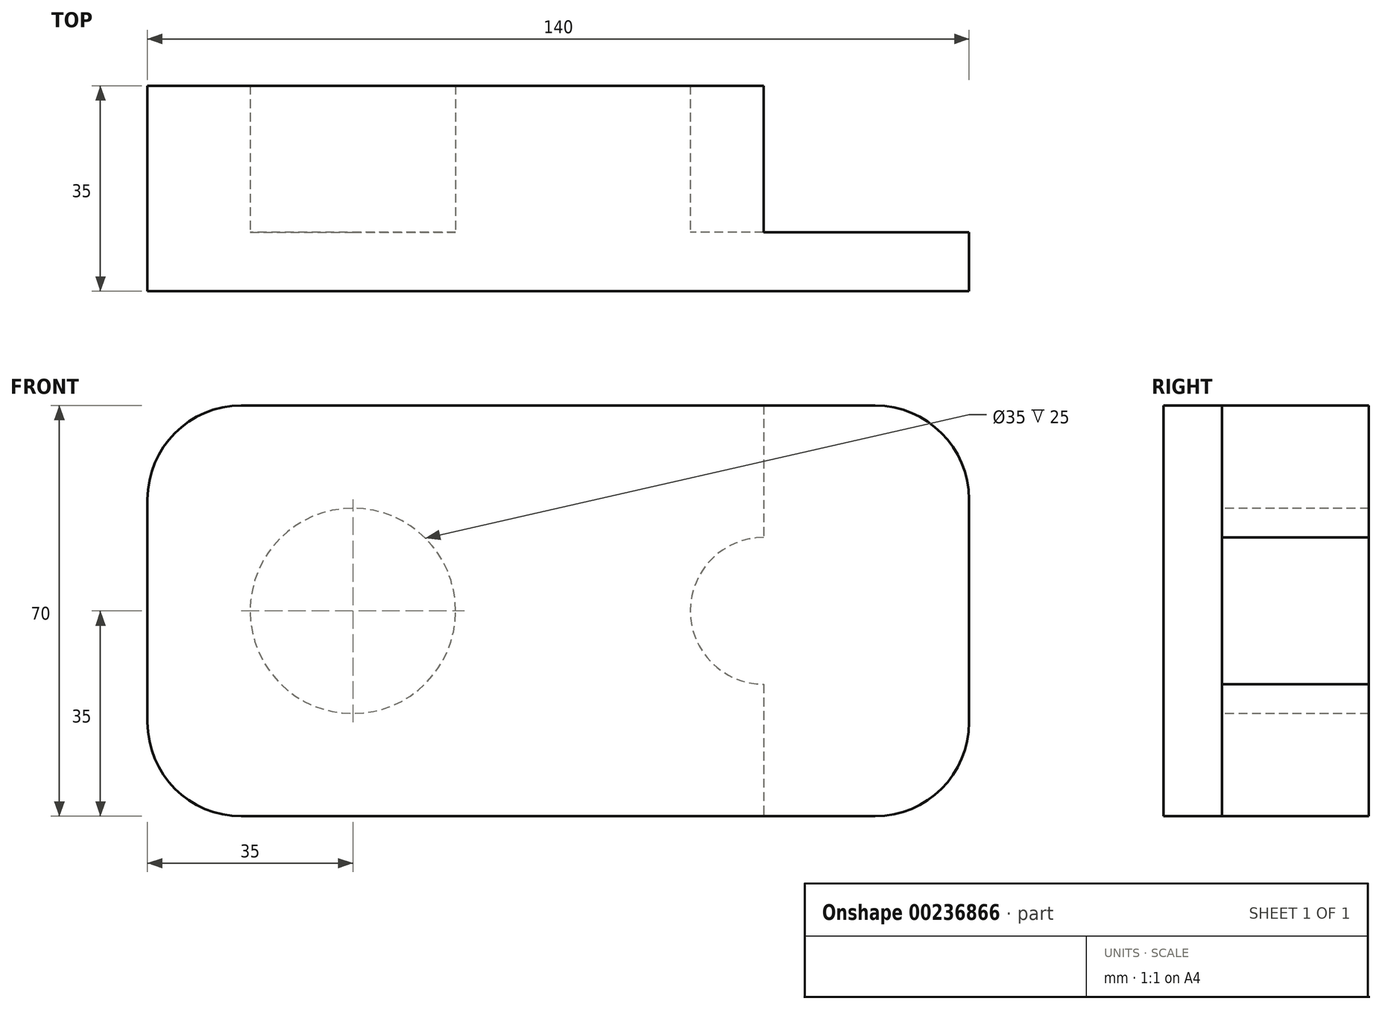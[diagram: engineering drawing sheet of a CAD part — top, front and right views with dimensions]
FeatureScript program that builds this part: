
annotation { "Feature Type Name" : "Feature", "Feature Type Description" : "" }
export const myFeature = defineFeature(function(context is Context, id is Id, definition is map)
    precondition{}
    {
        {
            var Q0;
            Q0=qCreatedBy(makeId("Front.planeOp"),FACE);
            var sketch = newSketch(context, id + "F0", { "sketchPlane" : qUnion([Q0])});
            skLineSegment(sketch, "E0", {"start": v(0, 0) * mm, "end": v(140, 0) * mm});
            skLineSegment(sketch, "E1", {"start": v(140, 0) * mm, "end": v(140, 70) * mm});
            skLineSegment(sketch, "E2", {"start": v(140, 70) * mm, "end": v(0, 70) * mm});
            skLineSegment(sketch, "E3", {"start": v(0, 70) * mm, "end": v(0, 0) * mm});
            skSolve(sketch);
        }
        {
            var Q0;
            Q0=makeQuery(id+"F0.imprint","IMPRINT",FACE,{"disambiguationData":[TD([[makeQuery(id+"F0.imprint","IMPRINT",EDGE,{"derivedFrom":sQuery(id+"F0.wireOp",EDGE,"E0")}),1.0]])]});
            extrude(context, id + "F1", {"entities" : qUnion([Q0]), "depth" : 10 * mm});
        }
        {
            var Q0;
            Q0=makeQuery(id+"F1.opExtrude","SWEPT_EDGE",EDGE,{"disambiguationData":[OSD([sQuery(id+"F0.wireOp",EDGE,"E0"),sQuery(id+"F0.wireOp",EDGE,"E3")])]});
            var Q1;
            Q1=makeQuery(id+"F1.opExtrude","SWEPT_EDGE",EDGE,{"disambiguationData":[OSD([sQuery(id+"F0.wireOp",EDGE,"E0"),sQuery(id+"F0.wireOp",EDGE,"E1")])]});
            var Q2;
            Q2=makeQuery(id+"F1.opExtrude","SWEPT_EDGE",EDGE,{"disambiguationData":[OSD([sQuery(id+"F0.wireOp",EDGE,"E1"),sQuery(id+"F0.wireOp",EDGE,"E2")])]});
            var Q3;
            Q3=makeQuery(id+"F1.opExtrude","SWEPT_EDGE",EDGE,{"disambiguationData":[OSD([sQuery(id+"F0.wireOp",EDGE,"E2"),sQuery(id+"F0.wireOp",EDGE,"E3")])]});
            fillet(context, id + "F2", {"entities" : qUnion([Q0, Q1, Q2, Q3]), "radius" : 16 * mm, "tangentPropagation" : true, "allowEdgeOverflow" : false});
        }
        {
            var Q0;
            Q0=makeQuery(id+"F1.opExtrude","CAP_FACE",FACE,{"disambiguationData":[OSD([sQuery(id+"F0.wireOp",EDGE,"E0"),sQuery(id+"F0.wireOp",EDGE,"E1"),sQuery(id+"F0.wireOp",EDGE,"E2"),sQuery(id+"F0.wireOp",EDGE,"E3")])],"isStart":true});
            var sketch = newSketch(context, id + "F3", { "sketchPlane" : qUnion([Q0])});
            skLineSegment(sketch, "E4", {"start": v(-140, 35) * mm, "end": v(0, 35) * mm});
            skLineSegment(sketch, "E5", {"start": v(-105, 70) * mm, "end": v(-105, 0) * mm});
            skLineSegment(sketch, "E6", {"start": v(-70, 70) * mm, "end": v(-70, 0) * mm, "construction": true});
            skCircle(sketch, "E7", {"center": v(-105, 35) * mm, "radius": 17.5 * mm});
            skCircle(sketch, "E8", {"center": v(-105, 35) * mm, "radius": 12.5 * mm});
            skLineSegment(sketch, "E9", {"start": v(-87.68, 37.5) * mm, "end": v(-70, 37.5) * mm});
            skLineSegment(sketch, "E10", {"start": v(-87.68, 32.5) * mm, "end": v(-70, 32.5) * mm});
            skCircle(sketch, "E11.MirrorC", {"center": v(-35, 35) * mm, "radius": 17.5 * mm});
            skCircle(sketch, "E12.MirrorC", {"center": v(-35, 35) * mm, "radius": 12.5 * mm});
            skLineSegment(sketch, "E13.MirrorCS", {"start": v(-52.32, 37.5) * mm, "end": v(-70, 37.5) * mm});
            skLineSegment(sketch, "E14.MirrorCS", {"start": v(-52.32, 32.5) * mm, "end": v(-70, 32.5) * mm});
            skSolve(sketch);
        }
        {
            var Q0;
            {var subQ2=sQuery(id+"F3.wireOp",EDGE,"E4");var subQ6=sQuery(id+"F3.wireOp",EDGE,"E8");var subQ8=makeQuery(id+"F3.imprint","INTERSECT",VERTEX,{"disambiguationData":[OD(1.0)],"derivedFrom":[subQ2,subQ6]});Q0=makeQuery(id+"F3.imprint","IMPRINT",FACE,{"disambiguationData":[TD([[makeQuery(id+"F3.imprint","IMPRINT",EDGE,{"disambiguationData":[TD([[subQ8,-1.0]])],"derivedFrom":subQ2}),1.0]])]});}
            var Q1;
            {var subQ0=sQuery(id+"F3.wireOp",EDGE,"E7");var subQ1=sQuery(id+"F3.wireOp",EDGE,"E4");var subQ2=makeQuery(id+"F3.imprint","INTERSECT",VERTEX,{"disambiguationData":[OD(0.0)],"derivedFrom":[subQ1,subQ0]});Q1=makeQuery(id+"F3.imprint","IMPRINT",FACE,{"disambiguationData":[TD([[makeQuery(id+"F3.imprint","IMPRINT",EDGE,{"disambiguationData":[TD([[subQ2,-1.0]])],"derivedFrom":subQ1}),1.0]])]});}
            var Q2;
            {var subQ0=sQuery(id+"F3.wireOp",EDGE,"E7");var subQ1=sQuery(id+"F3.wireOp",EDGE,"E4");var subQ2=makeQuery(id+"F3.imprint","INTERSECT",VERTEX,{"disambiguationData":[OD(0.0)],"derivedFrom":[subQ1,subQ0]});Q2=makeQuery(id+"F3.imprint","IMPRINT",FACE,{"disambiguationData":[TD([[makeQuery(id+"F3.imprint","IMPRINT",EDGE,{"disambiguationData":[TD([[subQ2,-1.0]])],"derivedFrom":subQ1}),-1.0]])]});}
            var Q3;
            {var subQ2=sQuery(id+"F3.wireOp",EDGE,"E4");var subQ4=sQuery(id+"F3.wireOp",EDGE,"E8");var subQ8=makeQuery(id+"F3.imprint","INTERSECT",VERTEX,{"disambiguationData":[OD(1.0)],"derivedFrom":[subQ2,subQ4]});Q3=makeQuery(id+"F3.imprint","IMPRINT",FACE,{"disambiguationData":[TD([[makeQuery(id+"F3.imprint","IMPRINT",EDGE,{"disambiguationData":[TD([[subQ8,-1.0]])],"derivedFrom":subQ2}),-1.0]])]});}
            var Q4;
            {var subQ0=sQuery(id+"F3.wireOp",EDGE,"E11.MirrorC");var subQ2=sQuery(id+"F3.wireOp",EDGE,"E4");var subQ7=makeQuery(id+"F3.imprint","INTERSECT",VERTEX,{"disambiguationData":[OD(0.0)],"derivedFrom":[subQ2,subQ0]});Q4=makeQuery(id+"F3.imprint","IMPRINT",FACE,{"disambiguationData":[TD([[makeQuery(id+"F3.imprint","IMPRINT",EDGE,{"disambiguationData":[TD([[subQ7,-1.0]])],"derivedFrom":subQ2}),1.0]])]});}
            var Q5;
            {var subQ0=sQuery(id+"F3.wireOp",EDGE,"E11.MirrorC");var subQ2=sQuery(id+"F3.wireOp",EDGE,"E4");var subQ3=makeQuery(id+"F3.imprint","INTERSECT",VERTEX,{"disambiguationData":[OD(0.0)],"derivedFrom":[subQ2,subQ0]});Q5=makeQuery(id+"F3.imprint","IMPRINT",FACE,{"disambiguationData":[TD([[makeQuery(id+"F3.imprint","IMPRINT",EDGE,{"disambiguationData":[TD([[subQ3,-1.0]])],"derivedFrom":subQ2}),-1.0]])]});}
            var Q6;
            {var subQ4=sQuery(id+"F3.wireOp",EDGE,"E9");Q6=makeQuery(id+"F3.imprint","IMPRINT",FACE,{"disambiguationData":[TD([[makeQuery(id+"F3.imprint","IMPRINT",EDGE,{"derivedFrom":subQ4}),-1.0]])]});}
            var Q7;
            {var subQ4=sQuery(id+"F3.wireOp",EDGE,"E10");Q7=makeQuery(id+"F3.imprint","IMPRINT",FACE,{"disambiguationData":[TD([[makeQuery(id+"F3.imprint","IMPRINT",EDGE,{"derivedFrom":subQ4}),1.0]])]});}
            extrude(context, id + "F4", {"entities" : qUnion([Q0, Q1, Q2, Q3, Q4, Q5, Q6, Q7]), "operationType" : NewBodyOperationType.ADD, "depth" : 25 * mm});
        }
    });
